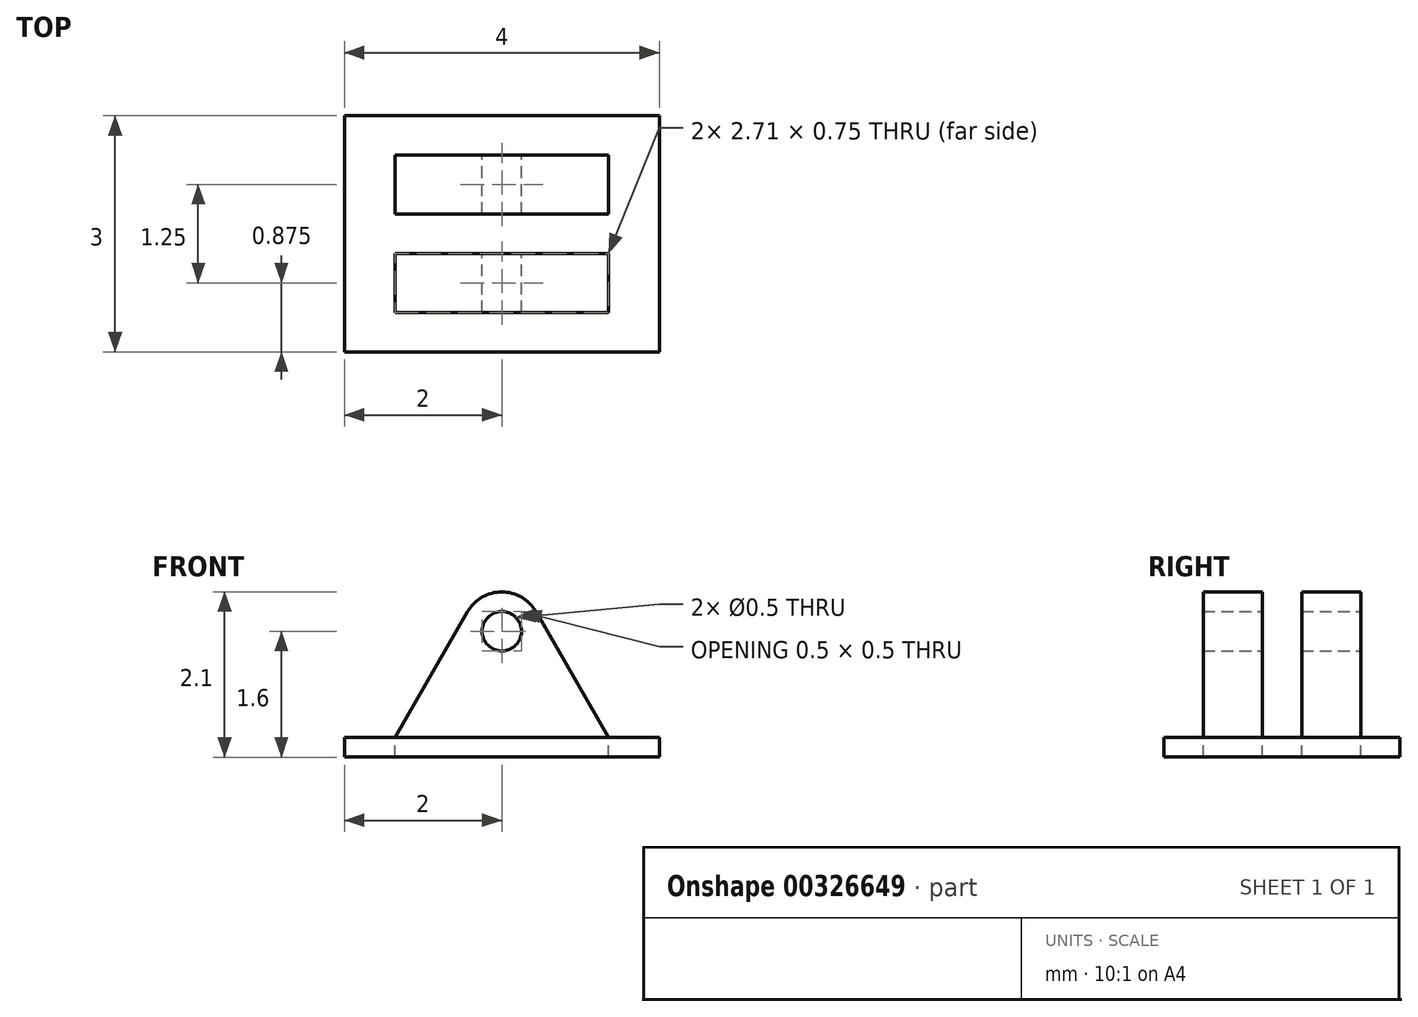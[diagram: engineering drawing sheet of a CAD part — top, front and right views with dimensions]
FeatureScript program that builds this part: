
annotation { "Feature Type Name" : "Feature", "Feature Type Description" : "" }
export const myFeature = defineFeature(function(context is Context, id is Id, definition is map)
    precondition{}
    {
        {
            var Q0;
            Q0=qCreatedBy(makeId("Front.planeOp"),FACE);
            var sketch = newSketch(context, id + "F0", { "sketchPlane" : qUnion([Q0])});
            skCircle(sketch, "E0", {"center": v(0, 0) * mm, "radius": 0.25 * mm});
            skLineSegment(sketch, "E1", {"start": v(-0.43, 0.25) * mm, "end": v(-1.36, -1.35) * mm});
            skLineSegment(sketch, "E2", {"start": v(1.36, -1.35) * mm, "end": v(0.43, 0.25) * mm});
            skArc(sketch, "E3.filletArc", {"start": v(0.43, 0.25) * mm, "mid": v(0, 0.5) * mm, "end": v(-0.43, 0.25) * mm});
            skLineSegment(sketch, "E4.bottom", {"start": v(1.36, -1.35) * mm, "end": v(-1.36, -1.35) * mm});
            skSolve(sketch);
        }
        {
            var Q0;
            Q0=makeQuery(id+"F0.imprint","IMPRINT",FACE,{"disambiguationData":[TD([[makeQuery(id+"F0.imprint","IMPRINT",EDGE,{"derivedFrom":sQuery(id+"F0.wireOp",EDGE,"E0")}),-1.0]])]});
            extrude(context, id + "F1", {"entities" : qUnion([Q0]), "offsetDistance" : 25 * mm, "depth" : 2 * mm});
        }
        {
            var Q0;
            Q0=qCreatedBy(makeId("Right.planeOp"),FACE);
            var sketch = newSketch(context, id + "F2", { "sketchPlane" : qUnion([Q0])});
            skLineSegment(sketch, "E5.0.0", {"start": v(0, 0.25) * mm, "end": v(0, 0.25) * mm});
            skLineSegment(sketch, "E5.0.1", {"start": v(-2, 0.25) * mm, "end": v(0, 0.25) * mm});
            skLineSegment(sketch, "E5.0.2", {"start": v(-2, 0.25) * mm, "end": v(-2, 0.25) * mm});
            skLineSegment(sketch, "E5.0.3", {"start": v(-2, 0.25) * mm, "end": v(0, 0.25) * mm});
            skLineSegment(sketch, "E6.bottom", {"start": v(-1.25, 1.85) * mm, "end": v(-0.75, 1.85) * mm});
            skLineSegment(sketch, "E6.top", {"start": v(-1.25, -1.35) * mm, "end": v(-0.75, -1.35) * mm});
            skLineSegment(sketch, "E6.left", {"start": v(-1.25, 1.85) * mm, "end": v(-1.25, -1.35) * mm});
            skLineSegment(sketch, "E6.right", {"start": v(-0.75, 1.85) * mm, "end": v(-0.75, -1.35) * mm});
            skPoint(sketch, "E6.middle", {"position": v(-1, 0.25) * mm});
            skPoint(sketch, "E7", {"position": v(-0.75, 0.25) * mm});
            skLineSegment(sketch, "E8.0.0", {"start": v(0, -1.35) * mm, "end": v(0, 0.25) * mm});
            skLineSegment(sketch, "E8.0.1", {"start": v(0, 0.25) * mm, "end": v(-2, 0.25) * mm});
            skLineSegment(sketch, "E8.0.2", {"start": v(-2, 0.25) * mm, "end": v(-2, -1.35) * mm});
            skLineSegment(sketch, "E8.0.3", {"start": v(-2, -1.35) * mm, "end": v(0, -1.35) * mm});
            skSolve(sketch);
        }
        {
            var Q0;
            {var subQ0=sQuery(id+"F2.wireOp",EDGE,"E6.bottom");Q0=makeQuery(id+"F2.imprint","IMPRINT",FACE,{"disambiguationData":[TD([[makeQuery(id+"F2.imprint","IMPRINT",EDGE,{"derivedFrom":subQ0}),-1.0]])]});}
            var Q1;
            {var subQ0=sQuery(id+"F2.wireOp",EDGE,"E8.0.3");var subQ1=sQuery(id+"F2.wireOp",EDGE,"E6.left");var subQ2=makeQuery(id+"F2.imprint","INTERSECT",VERTEX,{"derivedFrom":[subQ1,subQ0]});Q1=makeQuery(id+"F2.imprint","IMPRINT",FACE,{"disambiguationData":[TD([[makeQuery(id+"F2.imprint","IMPRINT",EDGE,{"disambiguationData":[TD([[subQ2,1.0]])],"derivedFrom":subQ1}),1.0]])]});}
            extrude(context, id + "F3", {"entities" : qUnion([Q0, Q1]), "operationType" : NewBodyOperationType.REMOVE, "endBound" : BoundingType.SYMMETRIC, "offsetDistance" : 25 * mm, "depth" : 25 * mm});
        }
        {
            var Q0;
            {var subQ0=sQuery(id+"F0.wireOp",EDGE,"E4.bottom");Q0=makeQuery(id+"F3.boolean.opBoolean","SPLIT",FACE,{"disambiguationData":[TD([makeQuery(id+"F3.opExtrude","SWEPT_FACE",FACE,{"disambiguationData":[OSD([sQuery(id+"F2.wireOp",EDGE,"E6.left")])]})])],"derivedFrom":makeQuery(id+"F1.opExtrude","SWEPT_FACE",FACE,{"disambiguationData":[OSD([subQ0])]})});}
            var sketch = newSketch(context, id + "F4", { "sketchPlane" : qUnion([Q0])});
            skLineSegment(sketch, "E9.0.0", {"start": v(1.36, 0) * mm, "end": v(1.36, 0.75) * mm});
            skLineSegment(sketch, "E9.0.1", {"start": v(1.36, 0.75) * mm, "end": v(-1.36, 0.75) * mm});
            skLineSegment(sketch, "E9.0.2", {"start": v(-1.36, 0.75) * mm, "end": v(-1.36, 0) * mm});
            skLineSegment(sketch, "E9.0.3", {"start": v(-1.36, 0) * mm, "end": v(1.36, 0) * mm});
            skLineSegment(sketch, "E10.0.0", {"start": v(-1.36, 1.25) * mm, "end": v(1.36, 1.25) * mm});
            skLineSegment(sketch, "E10.0.1", {"start": v(1.36, 1.25) * mm, "end": v(1.36, 2) * mm});
            skLineSegment(sketch, "E10.0.2", {"start": v(1.36, 2) * mm, "end": v(-1.36, 2) * mm});
            skLineSegment(sketch, "E10.0.3", {"start": v(-1.36, 2) * mm, "end": v(-1.36, 1.25) * mm});
            skLineSegment(sketch, "E11", {"start": v(1.36, 1.25) * mm, "end": v(1.36, 0.75) * mm, "construction": true});
            skPoint(sketch, "E12", {"position": v(0, 1.25) * mm});
            skLineSegment(sketch, "E13", {"start": v(1.36, 1) * mm, "end": v(0, 1) * mm, "construction": true});
            skLineSegment(sketch, "E14.bottom", {"start": v(2, 2.5) * mm, "end": v(-2, 2.5) * mm});
            skLineSegment(sketch, "E14.top", {"start": v(2, -0.5) * mm, "end": v(-2, -0.5) * mm});
            skLineSegment(sketch, "E14.left", {"start": v(2, 2.5) * mm, "end": v(2, -0.5) * mm});
            skLineSegment(sketch, "E14.right", {"start": v(-2, 2.5) * mm, "end": v(-2, -0.5) * mm});
            skPoint(sketch, "E14.middle", {"position": v(0, 1) * mm});
            skSolve(sketch);
        }
        {
            var Q0;
            Q0=makeQuery(id+"F4.imprint","IMPRINT",FACE,{"disambiguationData":[TD([[makeQuery(id+"F4.imprint","IMPRINT",EDGE,{"derivedFrom":sQuery(id+"F4.wireOp",EDGE,"E10.0.0")}),1.0]])]});
            extrude(context, id + "F5", {"entities" : qUnion([Q0]), "depth" : .25 * mm});
        }
    });
